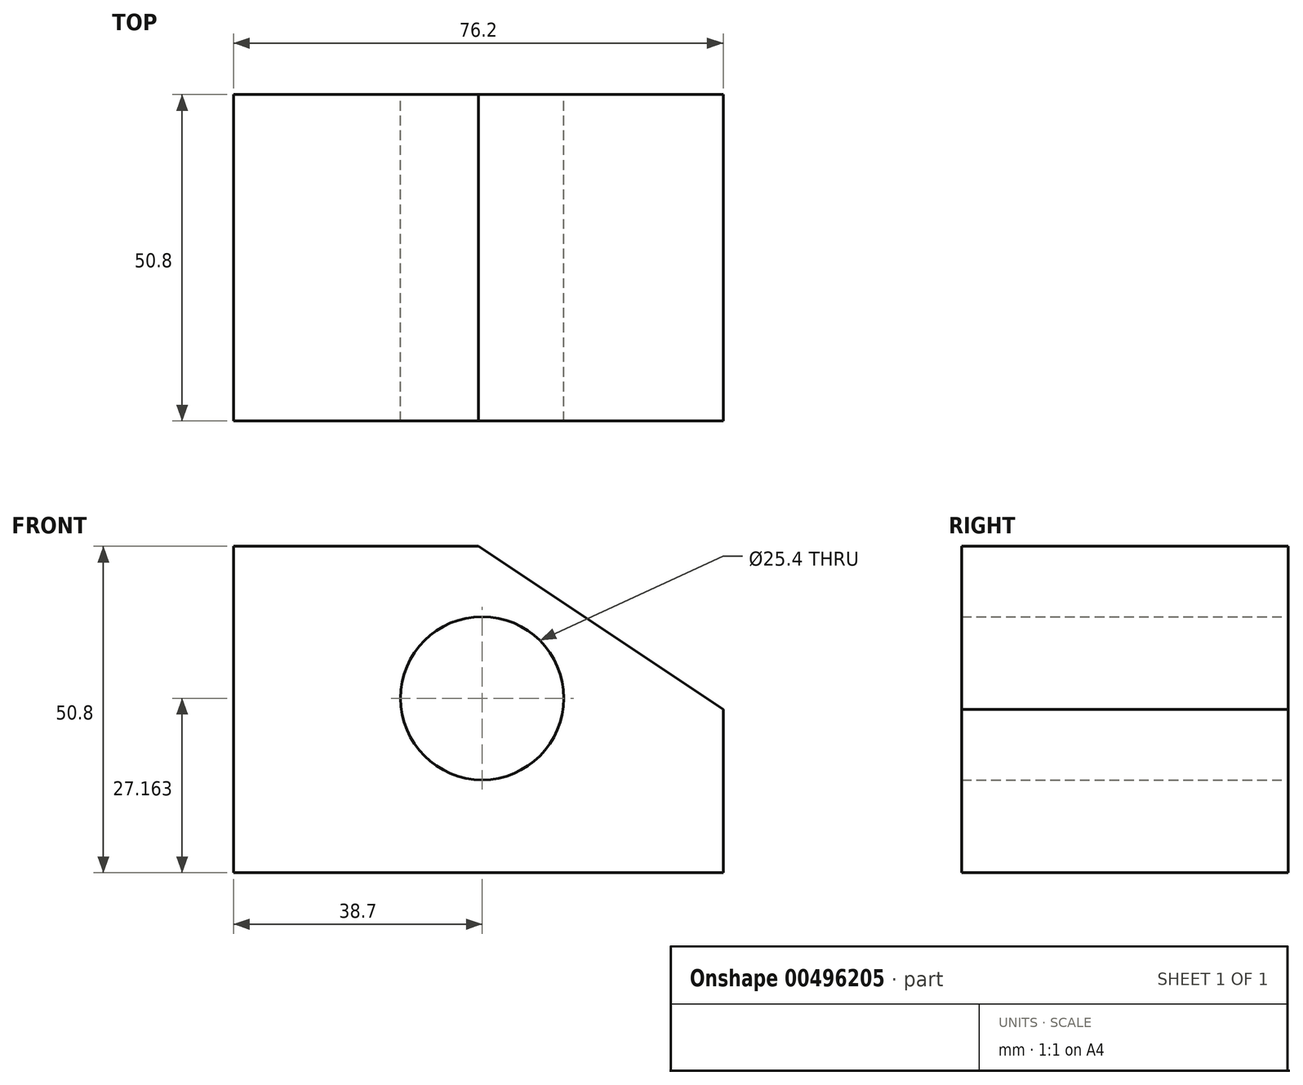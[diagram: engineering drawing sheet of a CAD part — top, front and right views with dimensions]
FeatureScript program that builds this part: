
annotation { "Feature Type Name" : "Feature", "Feature Type Description" : "" }
export const myFeature = defineFeature(function(context is Context, id is Id, definition is map)
    precondition{}
    {
        {
            var Q0;
            Q0=qCreatedBy(makeId("Front.planeOp"),FACE);
            var sketch = newSketch(context, id + "F0", { "sketchPlane" : qUnion([Q0])});
            skLineSegment(sketch, "E0", {"start": v(-43.91, 38.15) * mm, "end": v(-5.81, 38.15) * mm});
            skLineSegment(sketch, "E1", {"start": v(-43.91, -12.65) * mm, "end": v(-43.91, 38.15) * mm});
            skLineSegment(sketch, "E2", {"start": v(-43.91, -12.65) * mm, "end": v(32.29, -12.65) * mm});
            skLineSegment(sketch, "E3", {"start": v(32.29, -12.65) * mm, "end": v(32.29, 12.75) * mm});
            skLineSegment(sketch, "E4", {"start": v(-5.81, 38.15) * mm, "end": v(32.29, 12.75) * mm});
            skSolve(sketch);
        }
        {
            var Q0;
            Q0=makeQuery(id+"F0.imprint","IMPRINT",FACE,{"disambiguationData":[TD([[makeQuery(id+"F0.imprint","IMPRINT",EDGE,{"derivedFrom":sQuery(id+"F0.wireOp",EDGE,"E0")}),-1.0]])]});
            extrude(context, id + "F1", {"entities" : qUnion([Q0]), "depth" : 50.8 * mm});
        }
        {
            var Q0;
            Q0=qCreatedBy(makeId("Front.planeOp"),FACE);
            var sketch = newSketch(context, id + "F2", { "sketchPlane" : qUnion([Q0])});
            skCircle(sketch, "E5", {"center": v(-5.2, 14.51) * mm, "radius": 12.7 * mm});
            skSolve(sketch);
        }
        {
            var Q0;
            Q0 = qSketchRegion(id + "F2", true);
            extrude(context, id + "F3", {"entities" : qUnion([Q0]), "operationType" : NewBodyOperationType.REMOVE, "depth" : 60.45 * mm});
        }
    });
